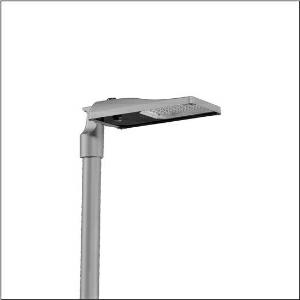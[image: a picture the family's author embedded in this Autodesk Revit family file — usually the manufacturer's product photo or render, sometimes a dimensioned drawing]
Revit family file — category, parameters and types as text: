
# Revit family: streetlight_sl_31_mini___st1_0a_5xh6d3at08ga_a0b3
name_source: partatom
category: Lighting Fixtures
units: mm (PartAtom-declared; Revit-internal decimal feet)

## family parameters
Cut with Voids When Loaded = No
Host = Face
Light Source = No
Part Type = Normal
Room Calculation Point = No
Round Connector Dimension = Use Diameter
Shared = No

## types (1)
- --- (1 x LED, 5880 lm, 39.3 W, 3000K)
    Apparent Load = 39 VA
    CIE Flux Codes = 37 72 97 100 100
    Color Rendering = 70
    Color Temperature = 3000K
    Default Elevation = 1800 mm
    Description = Streetlight SL 31 mini D4i mast luminaire for post-top, side-entry; light control with lens of PMMA; light distribution: ST1.0a, direct asymmetric distribution, for standard-compliant lighting for roads and squares; LED: luminous flux: 5.880lm, light colour: 730, colour temperature: 3000K; luminous efficacy: 149,6lm/W; control: pre-setting: logarithmic dimming characteristic, flexible luminous flux parameterisation, time-dependent luminous flux control, constant luminous flux control, power reduction, intelligent temperature release in ECG and LED module, overheat protection; luminaire housing, of diecast aluminium, Siteco® metallic grey (DB 702S), corrosivity category C5 high according to DIN EN ISO 12944; cover of toughened safety glass, transparent, opened without tools; mast flange of diecast aluminium, Siteco® metallic grey (DB 702S), spigot size: 76/60mm, mast flange included unmounted; with cable H07RN-F 2x 1.5mm², cable length: 6,5m, connection cable pre-assembled; mains connection: 220..240V, AC, 50/60Hz; power consumption (at start of service life): 39,3W / (at end of service life): 40,7W / (with reduced operation 50%): 18,1W; protection rating (complete): IP66; insulation class (complete): insulation class II (safety insulation); impact resistance: IK09; certification: CE, ENEC, ENEC+, VDE, UKCA, ZD4i; permissible operating ambient temperature for outdoor applications: -40..+50°C; packaging unit: 1 piece

Light Distribution: ST1.0a
    Height = 76 mm
    Lamp = 1 x LED
    Lamp Light Flux = 5880 lm
    Lamp Power = 39.3 W
    Lamp count = 1
    Length = 547 mm
    Luminous efficacy = 150 lm/W
    Manufacturer = Siteco
    ModVariant = No
    Model = 5XH6D3AT08GA
    Number of Poles = 1
    OnlyDefault = Yes
    Power Factor = 1
    Product Name = Streetlight SL 31 mini | ST1.0a
    Product group = mast luminaire | pylon top
    ProductGroupID = 6100
    Protection Class = Protection class II
    Protection Degree = IP 66
    RLX_Detail_Level = 1
    RLX_Emergency_Light_Flux = 0 lm
    RLX_Emergency_Type = 0
    RLX_Emergency_Type_DB = No
    RlxData = <blob elided: 39685 chars, md5=1dc12db9>
    Socket = socket
    Standby Power = 0 W
    System Light Flux = 5880 lm
    System Power = 39 W
    Type Comments = factory setting: luminous flux: 100 % | dim-lin: 254 | 798 mA
    Type Image = l_1300332.jpg
    URL = http://relux.com
    VarID = @adj_074267
    Voltage = 0 V
    Weight = 0.00 kg
    Width = 265 mm

## geometry (parser evidence)
native form markers: Blend x4, Sweep x10
no freeform markers — native parametric forms only
